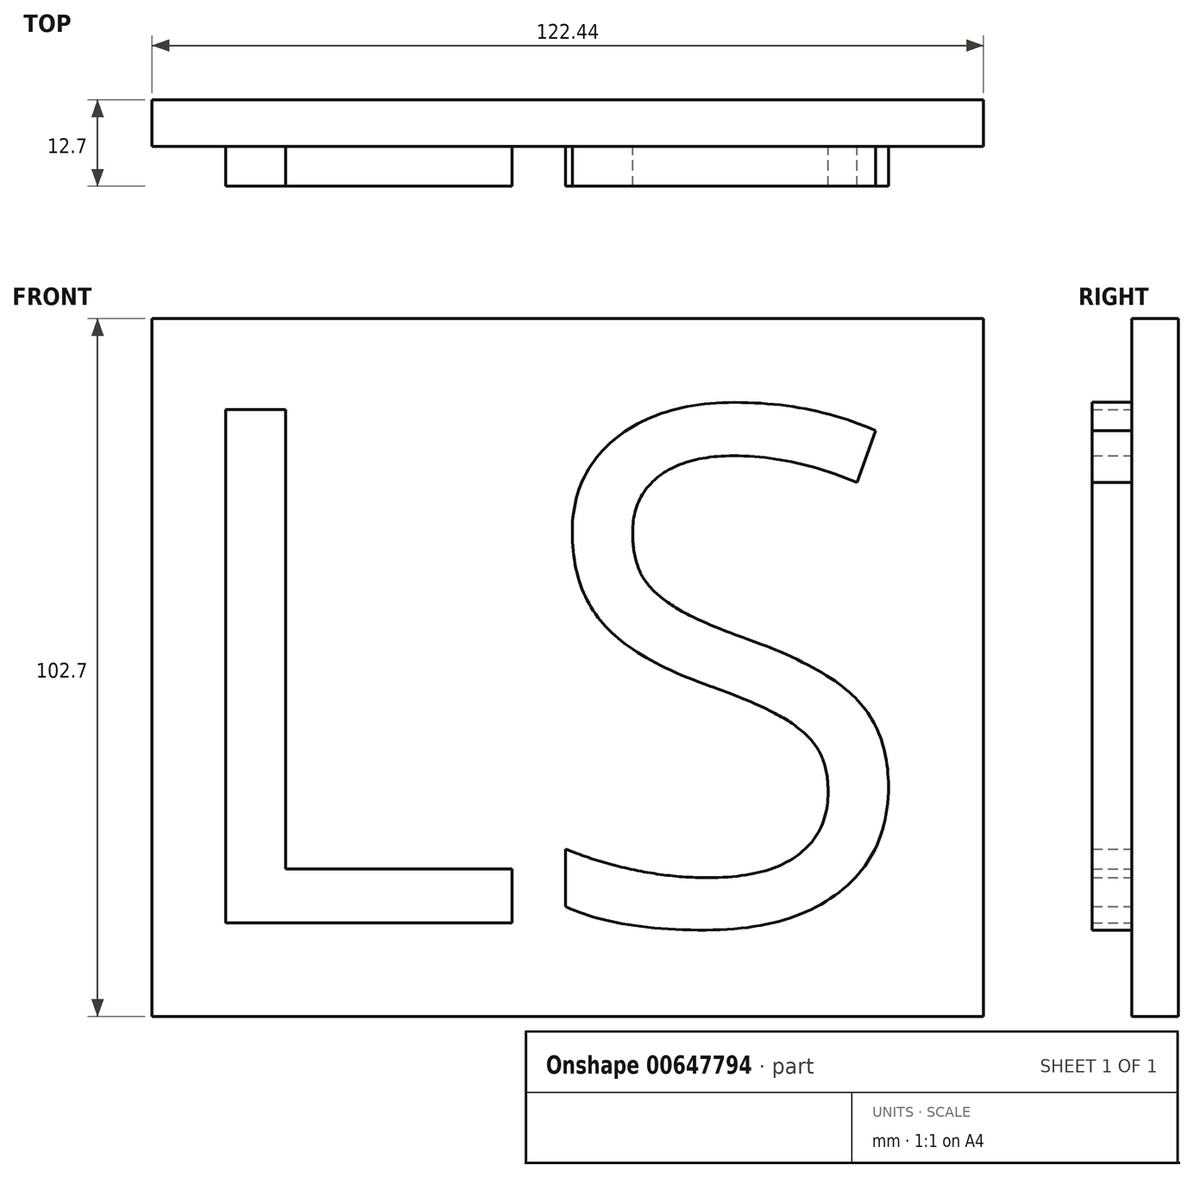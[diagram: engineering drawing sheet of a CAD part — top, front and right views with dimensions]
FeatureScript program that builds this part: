
annotation { "Feature Type Name" : "Feature", "Feature Type Description" : "" }
export const myFeature = defineFeature(function(context is Context, id is Id, definition is map)
    precondition{}
    {
        {
            var Q0;
            Q0=qCreatedBy(makeId("Front.planeOp"),FACE);
            var sketch = newSketch(context, id + "F0", { "sketchPlane" : qUnion([Q0])});
            skText(sketch, "E0", { "text": "LS", "fontName": "OpenSans-Regular.ttf"});
            const initialGuessF0  = {"E0": [-0.05169, -0.03766, 1, 0, 0.0762]};
            skSetInitialGuess(sketch, initialGuessF0);
            skSolve(sketch);
        }
        {
            var Q0;
            Q0 = qSketchRegion(id + "F0", true);
            extrude(context, id + "F1", {"entities" : qUnion([Q0]), "depth" : 12.7 * mm, "offsetDistance" : 25.4 * mm});
        }
        {
            var Q0;
            Q0=qCreatedBy(makeId("Front.planeOp"),FACE);
            var sketch = newSketch(context, id + "F2", { "sketchPlane" : qUnion([Q0])});
            skLineSegment(sketch, "E1.bottom", {"start": v(-52.21, 50.62) * mm, "end": v(70.15, 50.62) * mm});
            skLineSegment(sketch, "E1.top", {"start": v(-52.21, -51.61) * mm, "end": v(70.15, -51.61) * mm});
            skLineSegment(sketch, "E1.left", {"start": v(-52.21, 50.62) * mm, "end": v(-52.21, -51.61) * mm});
            skLineSegment(sketch, "E1.right", {"start": v(70.15, 50.62) * mm, "end": v(70.15, -51.61) * mm});
            skSolve(sketch);
        }
        {
            var Q0;
            Q0=makeQuery(id+"F2.imprint","IMPRINT",FACE,{"disambiguationData":[TD([[makeQuery(id+"F2.imprint","IMPRINT",EDGE,{"derivedFrom":sQuery(id+"F2.wireOp",EDGE,"E1.bottom")}),-1.0]])]});
            var sketch = newSketch(context, id + "F3", { "sketchPlane" : qUnion([Q0])});
            skLineSegment(sketch, "E2.bottom", {"start": v(-52.17, 51.3) * mm, "end": v(70.27, 51.3) * mm});
            skLineSegment(sketch, "E2.top", {"start": v(-52.17, -51.4) * mm, "end": v(70.27, -51.4) * mm});
            skLineSegment(sketch, "E2.left", {"start": v(-52.17, 51.3) * mm, "end": v(-52.17, -51.4) * mm});
            skLineSegment(sketch, "E2.right", {"start": v(70.27, 51.3) * mm, "end": v(70.27, -51.4) * mm});
            skSolve(sketch);
        }
        {
            var Q0;
            Q0 = qSketchRegion(id + "F3", true);
            extrude(context, id + "F4", {"entities" : qUnion([Q0]), "operationType" : NewBodyOperationType.ADD, "depth" : 6.86 * mm, "offsetDistance" : 25.4 * mm});
        }
    });
